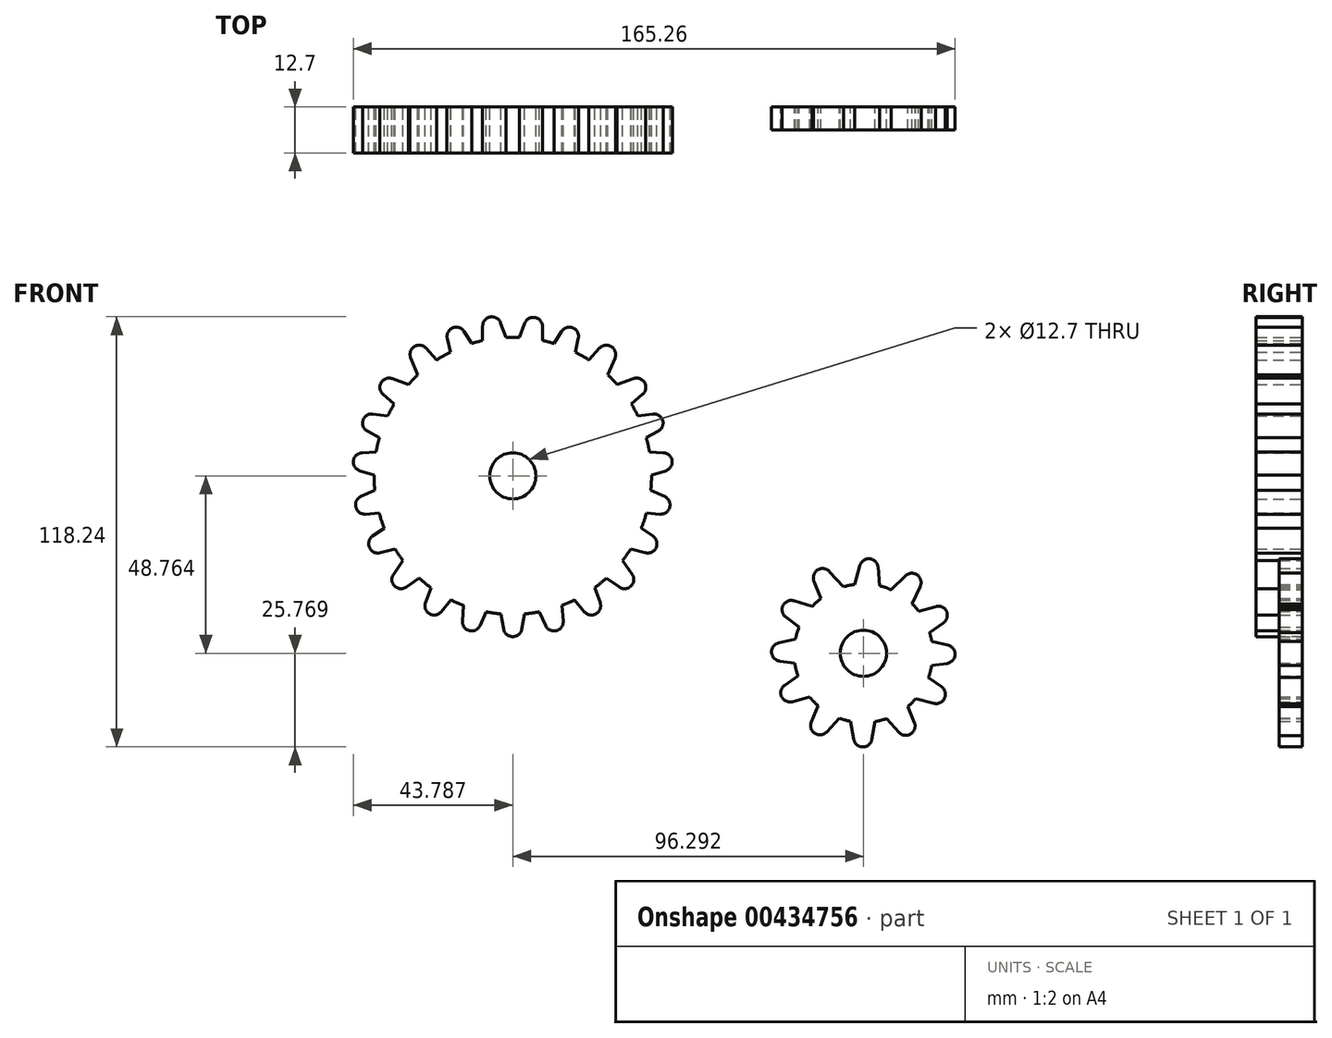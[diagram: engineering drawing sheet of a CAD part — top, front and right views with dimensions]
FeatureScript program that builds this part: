
annotation { "Feature Type Name" : "Feature", "Feature Type Description" : "" }
export const myFeature = defineFeature(function(context is Context, id is Id, definition is map)
    precondition{}
    {
        {
            var Q0;
            Q0=qCreatedBy(makeId("Front.planeOp"),FACE);
            var sketch = newSketch(context, id + "F0", { "sketchPlane" : qUnion([Q0])});
            skCircle(sketch, "E0", {"center": v(-72.8, 21.54) * mm, "radius": 38.1 * mm});
            skCircle(sketch, "E1", {"center": v(-72.8, 21.54) * mm, "radius": 6.35 * mm});
            skLineSegment(sketch, "E2", {"start": v(-76.16, 63.58) * mm, "end": v(-73.61, 56.57) * mm});
            skLineSegment(sketch, "E3", {"start": v(-73.61, 56.57) * mm, "end": v(-81.09, 55.25) * mm});
            skLineSegment(sketch, "E4", {"start": v(-81.09, 55.25) * mm, "end": v(-81.09, 62.71) * mm});
            skArc(sketch, "E5.filletArc", {"start": v(-79, 65.21) * mm, "mid": v(-80.5, 64.34) * mm, "end": v(-81.09, 62.71) * mm});
            skArc(sketch, "E6.filletArc", {"start": v(-76.16, 63.58) * mm, "mid": v(-77.28, 64.91) * mm, "end": v(-79, 65.21) * mm});
            skLineSegment(sketch, "E7.MirrorCS", {"start": v(-70.8, -13.35) * mm, "end": v(-78.36, -12.96) * mm});
            skLineSegment(sketch, "E8.MirrorCS", {"start": v(-70.32, -20.56) * mm, "end": v(-69.03, -13.22) * mm});
            skLineSegment(sketch, "E9.MirrorCS", {"start": v(-76.62, -13.22) * mm, "end": v(-75.33, -20.56) * mm});
            skArc(sketch, "E10.MirrorCS", {"start": v(-72.83, -22.66) * mm, "mid": v(-74.46, -22.06) * mm, "end": v(-75.33, -20.56) * mm});
            skArc(sketch, "E11.MirrorCS", {"start": v(-70.32, -20.56) * mm, "mid": v(-71.2, -22.06) * mm, "end": v(-72.83, -22.66) * mm});
            skLineSegment(sketch, "E12.MirrorCS", {"start": v(-80.44, -12.49) * mm, "end": v(-87.68, -10.2) * mm});
            skLineSegment(sketch, "E13.MirrorCS", {"start": v(-81.81, -19.62) * mm, "end": v(-78.7, -12.85) * mm});
            skLineSegment(sketch, "E14.MirrorCS", {"start": v(-86.04, -10.92) * mm, "end": v(-86.65, -18.35) * mm});
            skArc(sketch, "E15.MirrorCS", {"start": v(-84.76, -21.02) * mm, "mid": v(-86.2, -20.03) * mm, "end": v(-86.65, -18.35) * mm});
            skArc(sketch, "E16.MirrorCS", {"start": v(-81.81, -19.62) * mm, "mid": v(-83.03, -20.86) * mm, "end": v(-84.76, -21.02) * mm});
            skLineSegment(sketch, "E17.MirrorCS", {"start": v(-87.66, -10.11) * mm, "end": v(-94.23, -6.32) * mm});
            skLineSegment(sketch, "E18.MirrorCS", {"start": v(-92.45, -15.82) * mm, "end": v(-87.66, -10.11) * mm});
            skLineSegment(sketch, "E19.MirrorCS", {"start": v(-94.23, -6.32) * mm, "end": v(-96.78, -13.32) * mm});
            skArc(sketch, "E20.MirrorCS", {"start": v(-95.67, -16.4) * mm, "mid": v(-96.78, -15.06) * mm, "end": v(-96.78, -13.32) * mm});
            skArc(sketch, "E21.MirrorCS", {"start": v(-92.45, -15.82) * mm, "mid": v(-93.95, -16.7) * mm, "end": v(-95.67, -16.4) * mm});
            skLineSegment(sketch, "E22.MirrorCS", {"start": v(-95.92, -4.77) * mm, "end": v(-101.3, 0.6) * mm});
            skLineSegment(sketch, "E23.MirrorCS", {"start": v(-102.03, -9.05) * mm, "end": v(-95.92, -4.77) * mm});
            skLineSegment(sketch, "E24.MirrorCS", {"start": v(-101.3, 0.6) * mm, "end": v(-105.57, -5.51) * mm});
            skArc(sketch, "E25.MirrorCS", {"start": v(-105.28, -8.76) * mm, "mid": v(-106.02, -7.2) * mm, "end": v(-105.57, -5.51) * mm});
            skArc(sketch, "E26.MirrorCS", {"start": v(-102.03, -9.05) * mm, "mid": v(-103.7, -9.5) * mm, "end": v(-105.28, -8.76) * mm});
            skLineSegment(sketch, "E27.MirrorCS", {"start": v(-102, 2.33) * mm, "end": v(-105.21, 9.2) * mm});
            skLineSegment(sketch, "E28.MirrorCS", {"start": v(-109.2, 0.4) * mm, "end": v(-102, 2.33) * mm});
            skLineSegment(sketch, "E29.MirrorCS", {"start": v(-105.21, 9.2) * mm, "end": v(-111.32, 4.93) * mm});
            skArc(sketch, "E30.MirrorCS", {"start": v(-112.16, 1.77) * mm, "mid": v(-112.32, 3.5) * mm, "end": v(-111.32, 4.93) * mm});
            skArc(sketch, "E31.MirrorCS", {"start": v(-109.2, 0.4) * mm, "mid": v(-110.93, 0.55) * mm, "end": v(-112.16, 1.77) * mm});
            skLineSegment(sketch, "E32.MirrorCS", {"start": v(-105.82, 11.57) * mm, "end": v(-107.7, 18.93) * mm});
            skLineSegment(sketch, "E33.MirrorCS", {"start": v(-113.25, 11.01) * mm, "end": v(-105.82, 11.57) * mm});
            skLineSegment(sketch, "E34.MirrorCS", {"start": v(-107.7, 18.93) * mm, "end": v(-114.49, 15.86) * mm});
            skArc(sketch, "E35.MirrorCS", {"start": v(-115.9, 12.91) * mm, "mid": v(-115.73, 14.64) * mm, "end": v(-114.49, 15.86) * mm});
            skArc(sketch, "E36.MirrorCS", {"start": v(-113.25, 11.01) * mm, "mid": v(-114.92, 11.48) * mm, "end": v(-115.9, 12.91) * mm});
            skLineSegment(sketch, "E37.MirrorCS", {"start": v(-107.7, 20.68) * mm, "end": v(-106.72, 28.2) * mm});
            skLineSegment(sketch, "E38.MirrorCS", {"start": v(-114.82, 22.92) * mm, "end": v(-107.7, 20.68) * mm});
            skLineSegment(sketch, "E39.MirrorCS", {"start": v(-106.72, 28.2) * mm, "end": v(-114.16, 27.88) * mm});
            skArc(sketch, "E40.MirrorCS", {"start": v(-116.57, 25.67) * mm, "mid": v(-115.77, 27.21) * mm, "end": v(-114.16, 27.88) * mm});
            skArc(sketch, "E41.MirrorCS", {"start": v(-114.82, 22.92) * mm, "mid": v(-116.2, 23.98) * mm, "end": v(-116.57, 25.67) * mm});
            skLineSegment(sketch, "E42.MirrorCS", {"start": v(-37.9, 20.68) * mm, "end": v(-38.89, 28.2) * mm});
            skLineSegment(sketch, "E43.MirrorCS", {"start": v(-38.89, 28.2) * mm, "end": v(-31.44, 27.88) * mm});
            skArc(sketch, "E44.MirrorCS", {"start": v(-29.03, 25.67) * mm, "mid": v(-29.84, 27.21) * mm, "end": v(-31.44, 27.88) * mm});
            skArc(sketch, "E45.MirrorCS", {"start": v(-30.79, 22.92) * mm, "mid": v(-29.41, 23.98) * mm, "end": v(-29.03, 25.67) * mm});
            skLineSegment(sketch, "E46.MirrorCS", {"start": v(-30.79, 22.92) * mm, "end": v(-37.9, 20.68) * mm});
            skLineSegment(sketch, "E47.MirrorCS", {"start": v(-37.9, 18.93) * mm, "end": v(-31.12, 15.86) * mm});
            skLineSegment(sketch, "E48.MirrorCS", {"start": v(-39.79, 11.57) * mm, "end": v(-37.9, 18.93) * mm});
            skLineSegment(sketch, "E49.MirrorCS", {"start": v(-32.35, 11.01) * mm, "end": v(-39.79, 11.57) * mm});
            skArc(sketch, "E50.MirrorCS", {"start": v(-32.35, 11.01) * mm, "mid": v(-30.68, 11.48) * mm, "end": v(-29.7, 12.91) * mm});
            skArc(sketch, "E51.MirrorCS", {"start": v(-29.7, 12.91) * mm, "mid": v(-29.87, 14.64) * mm, "end": v(-31.12, 15.86) * mm});
            skLineSegment(sketch, "E52.MirrorCS", {"start": v(-43.6, 2.33) * mm, "end": v(-40.4, 9.2) * mm});
            skLineSegment(sketch, "E53.MirrorCS", {"start": v(-40.4, 9.2) * mm, "end": v(-34.29, 4.93) * mm});
            skArc(sketch, "E54.MirrorCS", {"start": v(-33.44, 1.77) * mm, "mid": v(-33.3, 3.5) * mm, "end": v(-34.29, 4.93) * mm});
            skArc(sketch, "E55.MirrorCS", {"start": v(-36.4, 0.4) * mm, "mid": v(-34.67, 0.55) * mm, "end": v(-33.44, 1.77) * mm});
            skLineSegment(sketch, "E56.MirrorCS", {"start": v(-36.4, 0.4) * mm, "end": v(-43.6, 2.33) * mm});
            skLineSegment(sketch, "E57.MirrorCS", {"start": v(-49.68, -4.77) * mm, "end": v(-44.3, 0.6) * mm});
            skLineSegment(sketch, "E58.MirrorCS", {"start": v(-43.58, -9.05) * mm, "end": v(-49.68, -4.77) * mm});
            skArc(sketch, "E59.MirrorCS", {"start": v(-43.58, -9.05) * mm, "mid": v(-41.9, -9.5) * mm, "end": v(-40.33, -8.76) * mm});
            skArc(sketch, "E60.MirrorCS", {"start": v(-40.33, -8.76) * mm, "mid": v(-39.6, -7.2) * mm, "end": v(-40.04, -5.51) * mm});
            skLineSegment(sketch, "E61.MirrorCS", {"start": v(-44.3, 0.6) * mm, "end": v(-40.04, -5.51) * mm});
            skLineSegment(sketch, "E62.MirrorCS", {"start": v(-57.95, -10.11) * mm, "end": v(-51.37, -6.32) * mm});
            skLineSegment(sketch, "E63.MirrorCS", {"start": v(-53.16, -15.82) * mm, "end": v(-57.95, -10.11) * mm});
            skArc(sketch, "E64.MirrorCS", {"start": v(-53.16, -15.82) * mm, "mid": v(-51.65, -16.7) * mm, "end": v(-49.94, -16.4) * mm});
            skArc(sketch, "E65.MirrorCS", {"start": v(-49.94, -16.4) * mm, "mid": v(-48.82, -15.06) * mm, "end": v(-48.82, -13.32) * mm});
            skLineSegment(sketch, "E66.MirrorCS", {"start": v(-51.37, -6.32) * mm, "end": v(-48.82, -13.32) * mm});
            skLineSegment(sketch, "E67.MirrorCS", {"start": v(-59.56, -10.92) * mm, "end": v(-58.95, -18.35) * mm});
            skLineSegment(sketch, "E68.MirrorCS", {"start": v(-65.17, -12.49) * mm, "end": v(-57.93, -10.2) * mm});
            skLineSegment(sketch, "E69.MirrorCS", {"start": v(-63.8, -19.62) * mm, "end": v(-66.9, -12.85) * mm});
            skArc(sketch, "E70.MirrorCS", {"start": v(-63.8, -19.62) * mm, "mid": v(-62.57, -20.86) * mm, "end": v(-60.84, -21.02) * mm});
            skArc(sketch, "E71.MirrorCS", {"start": v(-60.84, -21.02) * mm, "mid": v(-59.41, -20.03) * mm, "end": v(-58.95, -18.35) * mm});
            skLineSegment(sketch, "E72.MirrorCS", {"start": v(-106.07, 30.36) * mm, "end": v(-103.82, 37.6) * mm});
            skLineSegment(sketch, "E73.MirrorCS", {"start": v(-112.7, 33.77) * mm, "end": v(-106.07, 30.36) * mm});
            skLineSegment(sketch, "E74.MirrorCS", {"start": v(-103.82, 37.6) * mm, "end": v(-111.22, 38.55) * mm});
            skArc(sketch, "E75.MirrorCS", {"start": v(-113.96, 36.78) * mm, "mid": v(-112.91, 38.16) * mm, "end": v(-111.22, 38.55) * mm});
            skArc(sketch, "E76.MirrorCS", {"start": v(-112.7, 33.77) * mm, "mid": v(-113.88, 35.05) * mm, "end": v(-113.96, 36.78) * mm});
            skLineSegment(sketch, "E77.MirrorCS", {"start": v(-102.73, 39.14) * mm, "end": v(-98.94, 45.72) * mm});
            skLineSegment(sketch, "E78.MirrorCS", {"start": v(-108.44, 43.93) * mm, "end": v(-102.73, 39.14) * mm});
            skLineSegment(sketch, "E79.MirrorCS", {"start": v(-98.94, 45.72) * mm, "end": v(-105.94, 48.27) * mm});
            skArc(sketch, "E80.MirrorCS", {"start": v(-109, 47.15) * mm, "mid": v(-107.68, 48.27) * mm, "end": v(-105.94, 48.27) * mm});
            skArc(sketch, "E81.MirrorCS", {"start": v(-108.44, 43.93) * mm, "mid": v(-109.3, 45.44) * mm, "end": v(-109, 47.15) * mm});
            skLineSegment(sketch, "E82.MirrorCS", {"start": v(-98, 47.04) * mm, "end": v(-91.59, 51.12) * mm});
            skLineSegment(sketch, "E83.MirrorCS", {"start": v(-100.84, 53.93) * mm, "end": v(-98, 47.04) * mm});
            skLineSegment(sketch, "E84.MirrorCS", {"start": v(-91.59, 51.12) * mm, "end": v(-96.62, 56.62) * mm});
            skArc(sketch, "E85.MirrorCS", {"start": v(-99.86, 57.04) * mm, "mid": v(-98.16, 57.42) * mm, "end": v(-96.62, 56.62) * mm});
            skArc(sketch, "E86.MirrorCS", {"start": v(-100.84, 53.93) * mm, "mid": v(-100.92, 55.66) * mm, "end": v(-99.86, 57.04) * mm});
            skLineSegment(sketch, "E87.MirrorCS", {"start": v(-89.18, 52.04) * mm, "end": v(-82.17, 54.96) * mm});
            skLineSegment(sketch, "E88.MirrorCS", {"start": v(-90.8, 59.31) * mm, "end": v(-89.18, 52.04) * mm});
            skLineSegment(sketch, "E89.MirrorCS", {"start": v(-82.17, 54.96) * mm, "end": v(-86.19, 61.23) * mm});
            skArc(sketch, "E90.MirrorCS", {"start": v(-89.3, 62.2) * mm, "mid": v(-87.57, 62.29) * mm, "end": v(-86.19, 61.23) * mm});
            skArc(sketch, "E91.MirrorCS", {"start": v(-90.8, 59.31) * mm, "mid": v(-90.58, 61.03) * mm, "end": v(-89.3, 62.2) * mm});
            skLineSegment(sketch, "E92.MirrorCS", {"start": v(-39.53, 30.36) * mm, "end": v(-41.78, 37.6) * mm});
            skLineSegment(sketch, "E93.MirrorCS", {"start": v(-32.9, 33.77) * mm, "end": v(-39.53, 30.36) * mm});
            skArc(sketch, "E94.MirrorCS", {"start": v(-32.9, 33.77) * mm, "mid": v(-31.73, 35.05) * mm, "end": v(-31.64, 36.78) * mm});
            skArc(sketch, "E95.MirrorCS", {"start": v(-31.64, 36.78) * mm, "mid": v(-32.7, 38.16) * mm, "end": v(-34.39, 38.55) * mm});
            skLineSegment(sketch, "E96.MirrorCS", {"start": v(-41.78, 37.6) * mm, "end": v(-34.39, 38.55) * mm});
            skLineSegment(sketch, "E97.MirrorCS", {"start": v(-42.87, 39.14) * mm, "end": v(-46.67, 45.72) * mm});
            skLineSegment(sketch, "E98.MirrorCS", {"start": v(-37.16, 43.93) * mm, "end": v(-42.87, 39.14) * mm});
            skArc(sketch, "E99.MirrorCS", {"start": v(-37.16, 43.93) * mm, "mid": v(-36.3, 45.44) * mm, "end": v(-36.6, 47.15) * mm});
            skArc(sketch, "E100.MirrorCS", {"start": v(-36.6, 47.15) * mm, "mid": v(-37.93, 48.27) * mm, "end": v(-39.67, 48.27) * mm});
            skLineSegment(sketch, "E101.MirrorCS", {"start": v(-46.67, 45.72) * mm, "end": v(-39.67, 48.27) * mm});
            skLineSegment(sketch, "E102.MirrorCS", {"start": v(-47.61, 47.04) * mm, "end": v(-54.02, 51.12) * mm});
            skLineSegment(sketch, "E103.MirrorCS", {"start": v(-54.02, 51.12) * mm, "end": v(-48.98, 56.62) * mm});
            skLineSegment(sketch, "E104.MirrorCS", {"start": v(-44.76, 53.93) * mm, "end": v(-47.61, 47.04) * mm});
            skArc(sketch, "E105.MirrorCS", {"start": v(-44.76, 53.93) * mm, "mid": v(-44.69, 55.66) * mm, "end": v(-45.75, 57.04) * mm});
            skArc(sketch, "E106.MirrorCS", {"start": v(-45.75, 57.04) * mm, "mid": v(-47.44, 57.42) * mm, "end": v(-48.98, 56.62) * mm});
            skLineSegment(sketch, "E107.MirrorCS", {"start": v(-56.43, 52.04) * mm, "end": v(-63.43, 54.96) * mm});
            skLineSegment(sketch, "E108.MirrorCS", {"start": v(-63.43, 54.96) * mm, "end": v(-59.42, 61.23) * mm});
            skLineSegment(sketch, "E109.MirrorCS", {"start": v(-54.8, 59.31) * mm, "end": v(-56.43, 52.04) * mm});
            skArc(sketch, "E110.MirrorCS", {"start": v(-54.8, 59.31) * mm, "mid": v(-55.02, 61.03) * mm, "end": v(-56.3, 62.2) * mm});
            skArc(sketch, "E111.MirrorCS", {"start": v(-56.3, 62.2) * mm, "mid": v(-58.04, 62.29) * mm, "end": v(-59.42, 61.23) * mm});
            skLineSegment(sketch, "E112.MirrorCS", {"start": v(-72.1, 56.43) * mm, "end": v(-64.63, 55.1) * mm});
            skLineSegment(sketch, "E113.MirrorCS", {"start": v(-69.55, 63.43) * mm, "end": v(-72.1, 56.43) * mm});
            skLineSegment(sketch, "E114.MirrorCS", {"start": v(-64.63, 55.1) * mm, "end": v(-64.63, 62.56) * mm});
            skArc(sketch, "E115.MirrorCS", {"start": v(-66.72, 65.06) * mm, "mid": v(-65.22, 64.2) * mm, "end": v(-64.63, 62.56) * mm});
            skArc(sketch, "E116.MirrorCS", {"start": v(-69.55, 63.43) * mm, "mid": v(-68.44, 64.76) * mm, "end": v(-66.72, 65.06) * mm});
            skSolve(sketch);
        }
        {
            var Q0;
            Q0 = qSketchRegion(id + "F0", true);
            extrude(context, id + "F1", {"entities" : qUnion([Q0]), "depth" : 12.7 * mm});
        }
        {
            var Q0;
            Q0=qCreatedBy(makeId("Front.planeOp"),FACE);
            var sketch = newSketch(context, id + "F2", { "sketchPlane" : qUnion([Q0])});
            skCircle(sketch, "E117", {"center": v(23.49, -27.22) * mm, "radius": 19.05 * mm});
            skCircle(sketch, "E118", {"center": v(23.49, -27.22) * mm, "radius": 6.35 * mm});
            skLineSegment(sketch, "E119.MirrorCS", {"start": v(19.54, -43.54) * mm, "end": v(27.13, -43.55) * mm});
            skLineSegment(sketch, "E120.MirrorCS", {"start": v(20.83, -50.89) * mm, "end": v(19.54, -43.54) * mm});
            skArc(sketch, "E121.MirrorCS", {"start": v(20.83, -50.89) * mm, "mid": v(21.7, -52.4) * mm, "end": v(23.33, -52.99) * mm});
            skArc(sketch, "E122.MirrorCS", {"start": v(23.33, -52.99) * mm, "mid": v(24.96, -52.4) * mm, "end": v(25.83, -50.89) * mm});
            skLineSegment(sketch, "E123.MirrorCS", {"start": v(27.13, -43.55) * mm, "end": v(25.83, -50.89) * mm});
            skLineSegment(sketch, "E124.MirrorCS", {"start": v(12, -39.27) * mm, "end": v(18.42, -43.32) * mm});
            skLineSegment(sketch, "E125.MirrorCS", {"start": v(9.18, -46.17) * mm, "end": v(12, -39.27) * mm});
            skArc(sketch, "E126.MirrorCS", {"start": v(9.18, -46.17) * mm, "mid": v(9.11, -47.9) * mm, "end": v(10.18, -49.27) * mm});
            skArc(sketch, "E127.MirrorCS", {"start": v(10.18, -49.27) * mm, "mid": v(11.88, -49.64) * mm, "end": v(13.41, -48.83) * mm});
            skLineSegment(sketch, "E128.MirrorCS", {"start": v(18.42, -43.32) * mm, "end": v(13.41, -48.83) * mm});
            skLineSegment(sketch, "E129.MirrorCS", {"start": v(7.98, -31.74) * mm, "end": v(11.18, -38.62) * mm});
            skLineSegment(sketch, "E130.MirrorCS", {"start": v(1.87, -36.01) * mm, "end": v(7.98, -31.74) * mm});
            skArc(sketch, "E131.MirrorCS", {"start": v(1.87, -36.01) * mm, "mid": v(0.87, -37.43) * mm, "end": v(1.02, -39.16) * mm});
            skArc(sketch, "E132.MirrorCS", {"start": v(1.02, -39.16) * mm, "mid": v(2.25, -40.4) * mm, "end": v(3.98, -40.55) * mm});
            skLineSegment(sketch, "E133.MirrorCS", {"start": v(11.18, -38.62) * mm, "end": v(3.98, -40.55) * mm});
            skLineSegment(sketch, "E134.MirrorCS", {"start": v(7.52, -22.75) * mm, "end": v(7.86, -30.34) * mm});
            skLineSegment(sketch, "E135.MirrorCS", {"start": v(0.24, -24.38) * mm, "end": v(7.52, -22.75) * mm});
            skArc(sketch, "E136.MirrorCS", {"start": v(0.24, -24.38) * mm, "mid": v(-1.22, -25.31) * mm, "end": v(-1.74, -26.97) * mm});
            skArc(sketch, "E137.MirrorCS", {"start": v(-1.74, -26.97) * mm, "mid": v(-1.08, -28.57) * mm, "end": v(0.47, -29.37) * mm});
            skLineSegment(sketch, "E138.MirrorCS", {"start": v(7.86, -30.34) * mm, "end": v(0.47, -29.37) * mm});
            skLineSegment(sketch, "E139", {"start": v(4.44, -27.22) * mm, "end": v(42.54, -27.22) * mm});
            skLineSegment(sketch, "E140", {"start": v(23.49, -8.17) * mm, "end": v(23.49, -46.27) * mm});
            skLineSegment(sketch, "E141.MirrorCS", {"start": v(34.67, -39.42) * mm, "end": v(28.25, -43.47) * mm});
            skLineSegment(sketch, "E142.MirrorCS", {"start": v(28.25, -43.47) * mm, "end": v(33.26, -48.99) * mm});
            skArc(sketch, "E143.MirrorCS", {"start": v(36.5, -49.43) * mm, "mid": v(34.8, -49.8) * mm, "end": v(33.26, -48.99) * mm});
            skArc(sketch, "E144.MirrorCS", {"start": v(37.5, -46.32) * mm, "mid": v(37.56, -48.05) * mm, "end": v(36.5, -49.43) * mm});
            skLineSegment(sketch, "E145.MirrorCS", {"start": v(37.5, -46.32) * mm, "end": v(34.67, -39.42) * mm});
            skLineSegment(sketch, "E146.MirrorCS", {"start": v(38.82, -32.18) * mm, "end": v(35.61, -39.06) * mm});
            skLineSegment(sketch, "E147.MirrorCS", {"start": v(35.61, -39.06) * mm, "end": v(42.82, -40.99) * mm});
            skArc(sketch, "E148.MirrorCS", {"start": v(45.77, -39.6) * mm, "mid": v(44.55, -40.83) * mm, "end": v(42.82, -40.99) * mm});
            skArc(sketch, "E149.MirrorCS", {"start": v(44.93, -36.45) * mm, "mid": v(45.92, -37.87) * mm, "end": v(45.77, -39.6) * mm});
            skLineSegment(sketch, "E150.MirrorCS", {"start": v(44.93, -36.45) * mm, "end": v(38.82, -32.18) * mm});
            skLineSegment(sketch, "E151.MirrorCS", {"start": v(39.07, -30.97) * mm, "end": v(46.46, -30) * mm});
            skLineSegment(sketch, "E152.MirrorCS", {"start": v(39.41, -23.39) * mm, "end": v(39.07, -30.97) * mm});
            skLineSegment(sketch, "E153.MirrorCS", {"start": v(46.69, -25.01) * mm, "end": v(39.41, -23.39) * mm});
            skArc(sketch, "E154.MirrorCS", {"start": v(46.69, -25.01) * mm, "mid": v(48.15, -25.95) * mm, "end": v(48.67, -27.6) * mm});
            skArc(sketch, "E155.MirrorCS", {"start": v(48.67, -27.6) * mm, "mid": v(48, -29.2) * mm, "end": v(46.46, -30) * mm});
            skLineSegment(sketch, "E156.MirrorCS", {"start": v(11.56, -14.96) * mm, "end": v(8.15, -21.74) * mm});
            skLineSegment(sketch, "E157.MirrorCS", {"start": v(4.42, -12.81) * mm, "end": v(11.56, -14.96) * mm});
            skArc(sketch, "E158.MirrorCS", {"start": v(4.42, -12.81) * mm, "mid": v(2.69, -12.91) * mm, "end": v(1.42, -14.1) * mm});
            skArc(sketch, "E159.MirrorCS", {"start": v(1.42, -14.1) * mm, "mid": v(1.22, -15.83) * mm, "end": v(2.17, -17.28) * mm});
            skLineSegment(sketch, "E160.MirrorCS", {"start": v(8.15, -21.74) * mm, "end": v(2.17, -17.28) * mm});
            skLineSegment(sketch, "E161.MirrorCS", {"start": v(19.17, -10.26) * mm, "end": v(12.76, -14.32) * mm});
            skLineSegment(sketch, "E162.MirrorCS", {"start": v(14.15, -4.75) * mm, "end": v(19.17, -10.26) * mm});
            skArc(sketch, "E163.MirrorCS", {"start": v(14.15, -4.75) * mm, "mid": v(12.6, -3.94) * mm, "end": v(10.91, -4.31) * mm});
            skArc(sketch, "E164.MirrorCS", {"start": v(10.91, -4.31) * mm, "mid": v(9.85, -5.69) * mm, "end": v(9.92, -7.43) * mm});
            skLineSegment(sketch, "E165.MirrorCS", {"start": v(12.76, -14.32) * mm, "end": v(9.92, -7.43) * mm});
            skLineSegment(sketch, "E166.MirrorCS", {"start": v(28.16, -11) * mm, "end": v(20.6, -10.34) * mm});
            skLineSegment(sketch, "E167.MirrorCS", {"start": v(27.52, -3.58) * mm, "end": v(28.16, -11) * mm});
            skArc(sketch, "E168.MirrorCS", {"start": v(27.52, -3.58) * mm, "mid": v(26.78, -2) * mm, "end": v(25.2, -1.27) * mm});
            skArc(sketch, "E169.MirrorCS", {"start": v(25.2, -1.27) * mm, "mid": v(23.53, -1.72) * mm, "end": v(22.53, -3.14) * mm});
            skLineSegment(sketch, "E170.MirrorCS", {"start": v(20.6, -10.34) * mm, "end": v(22.53, -3.14) * mm});
            skLineSegment(sketch, "E171.MirrorCS", {"start": v(35.93, -15.6) * mm, "end": v(29.72, -11.24) * mm});
            skLineSegment(sketch, "E172.MirrorCS", {"start": v(39.1, -8.85) * mm, "end": v(35.93, -15.6) * mm});
            skArc(sketch, "E173.MirrorCS", {"start": v(39.1, -8.85) * mm, "mid": v(39.24, -7.12) * mm, "end": v(38.25, -5.7) * mm});
            skArc(sketch, "E174.MirrorCS", {"start": v(38.25, -5.7) * mm, "mid": v(36.57, -5.24) * mm, "end": v(35, -5.98) * mm});
            skLineSegment(sketch, "E175.MirrorCS", {"start": v(29.72, -11.24) * mm, "end": v(35, -5.98) * mm});
            skLineSegment(sketch, "E176.MirrorCS", {"start": v(39.3, -23.22) * mm, "end": v(36.1, -16.33) * mm});
            skLineSegment(sketch, "E177.MirrorCS", {"start": v(45.41, -18.95) * mm, "end": v(39.3, -23.22) * mm});
            skArc(sketch, "E178.MirrorCS", {"start": v(45.41, -18.95) * mm, "mid": v(46.52, -17.18) * mm, "end": v(46, -15.16) * mm});
            skArc(sketch, "E179.MirrorCS", {"start": v(46, -15.16) * mm, "mid": v(44.77, -14.38) * mm, "end": v(43.3, -14.41) * mm});
            skLineSegment(sketch, "E180.MirrorCS", {"start": v(36.1, -16.33) * mm, "end": v(43.3, -14.41) * mm});
            skSolve(sketch);
        }
        {
            var Q0;
            Q0 = qSketchRegion(id + "F2", true);
            extrude(context, id + "F3", {"entities" : qUnion([Q0]), "depth" : 6.35 * mm});
        }
    });
